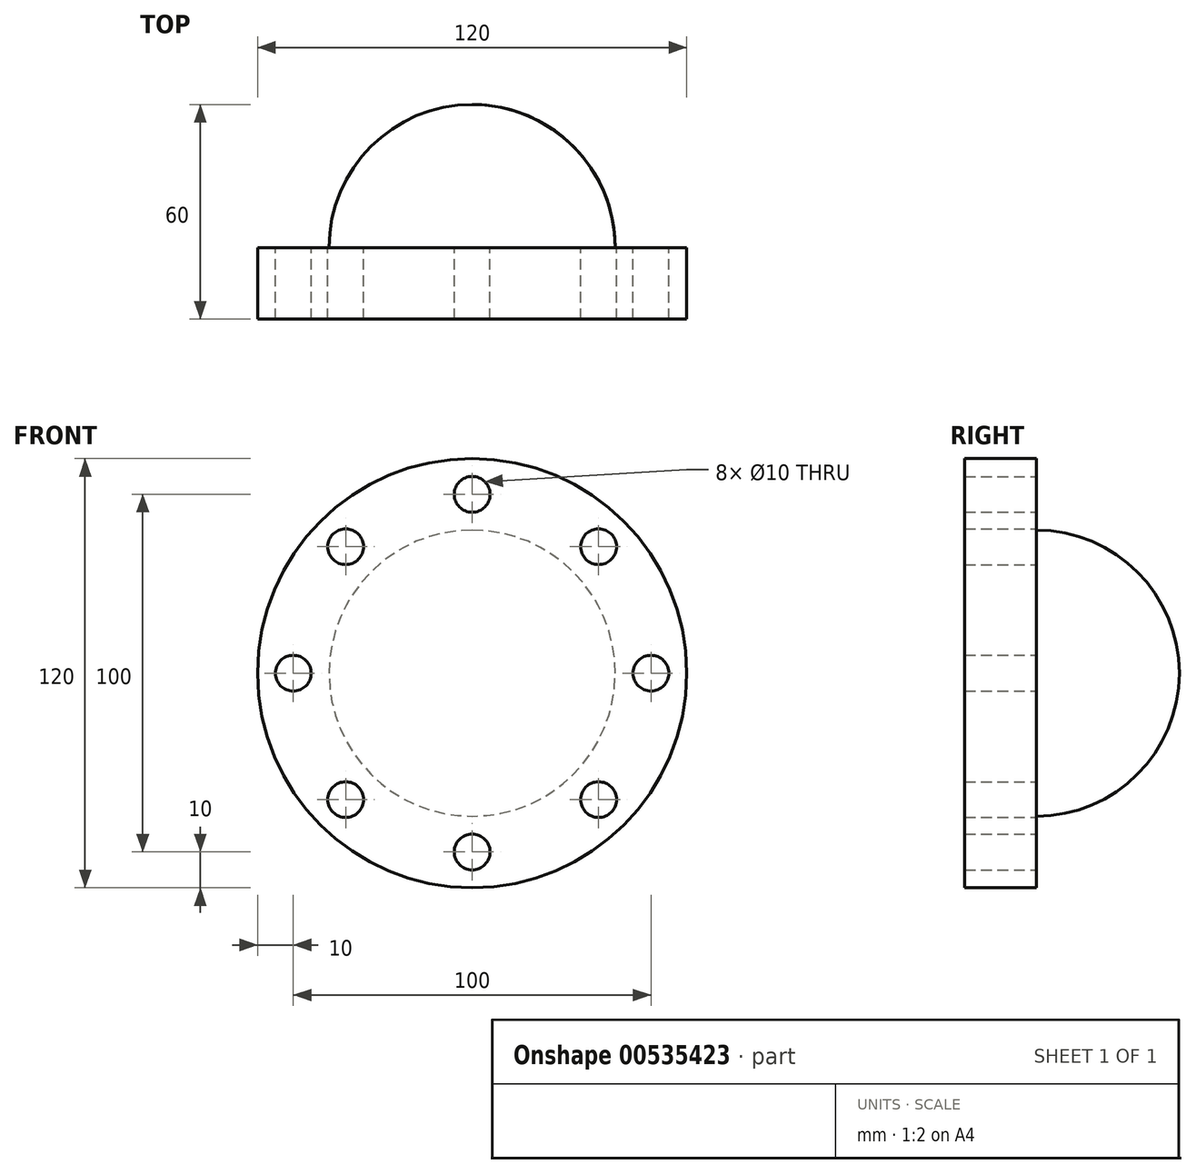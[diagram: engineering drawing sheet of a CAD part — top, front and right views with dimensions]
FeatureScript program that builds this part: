
annotation { "Feature Type Name" : "Feature", "Feature Type Description" : "" }
export const myFeature = defineFeature(function(context is Context, id is Id, definition is map)
    precondition{}
    {
        {
            var Q0;
            Q0=qCreatedBy(makeId("Front.planeOp"),FACE);
            var sketch = newSketch(context, id + "F0", { "sketchPlane" : qUnion([Q0])});
            skCircle(sketch, "E0", {"center": v(0, 0) * mm, "radius": 60 * mm});
            skCircle(sketch, "E1", {"center": v(0, 50) * mm, "radius": 5 * mm});
            skCircle(sketch, "E2.1.0", {"center": v(35.36, 35.36) * mm, "radius": 5 * mm});
            skCircle(sketch, "E2.2.0", {"center": v(50, 0) * mm, "radius": 5 * mm});
            skCircle(sketch, "E2.3.0", {"center": v(35.36, -35.36) * mm, "radius": 5 * mm});
            skCircle(sketch, "E2.4.0", {"center": v(0, -50) * mm, "radius": 5 * mm});
            skCircle(sketch, "E2.5.0", {"center": v(-35.36, -35.36) * mm, "radius": 5 * mm});
            skCircle(sketch, "E2.6.0", {"center": v(-50, 0) * mm, "radius": 5 * mm});
            skCircle(sketch, "E2.7.0", {"center": v(-35.36, 35.36) * mm, "radius": 5 * mm});
            skLineSegment(sketch, "E2.anchor1", {"start": v(0, 0) * mm, "end": v(0, 50) * mm, "construction": true});
            skLineSegment(sketch, "E2.anchor2", {"start": v(0, 0) * mm, "end": v(-35.36, 35.36) * mm, "construction": true});
            skSolve(sketch);
        }
        {
            var Q0;
            Q0 = qSketchRegion(id + "F0", true);
            extrude(context, id + "F1", {"entities" : qUnion([Q0]), "depth" : 20 * mm, "offsetDistance" : 25 * mm});
        }
        {
            var Q0;
            Q0=qCreatedBy(makeId("Top.planeOp"),FACE);
            var sketch = newSketch(context, id + "F2", { "sketchPlane" : qUnion([Q0])});
            skLineSegment(sketch, "E3", {"start": v(60, 0) * mm, "end": v(60, -20) * mm});
            skLineSegment(sketch, "E4", {"start": v(-60, -20) * mm, "end": v(-60, 0) * mm});
            skArc(sketch, "E5", {"start": v(0, 40) * mm, "mid": v(-28.28, 28.28) * mm, "end": v(-40, 0) * mm});
            skLineSegment(sketch, "E6", {"start": v(0, 40) * mm, "end": v(0, 0) * mm});
            skLineSegment(sketch, "E7", {"start": v(0, 0) * mm, "end": v(-40, 0) * mm});
            skSolve(sketch);
        }
        {
            var Q0;
            Q0=makeQuery(id+"F2.imprint","IMPRINT",FACE,{"disambiguationData":[TD([[makeQuery(id+"F2.imprint","IMPRINT",EDGE,{"derivedFrom":sQuery(id+"F2.wireOp",EDGE,"E5")}),1.0]])]});
            var Q1;
            Q1=sQuery(id+"F2.wireOp",EDGE,"E6");
            revolve(context, id + "F3", {"operationType" : NewBodyOperationType.ADD, "entities" : qUnion([Q0]), "axis" : qUnion([Q1]), "revolveType" : RevolveType.FULL});
        }
    });
